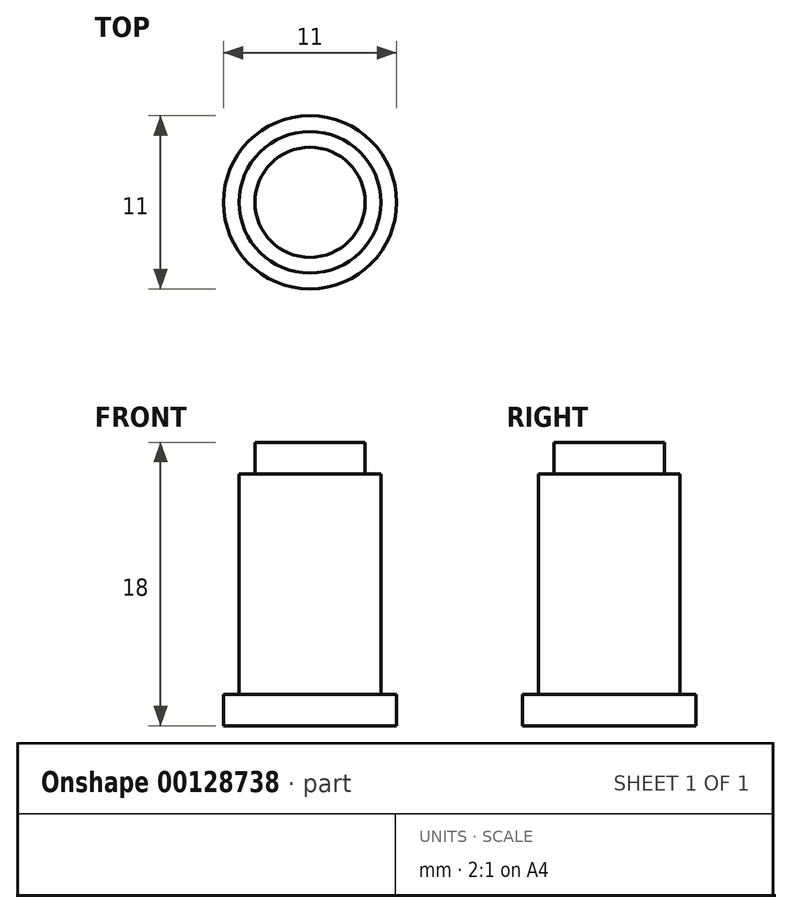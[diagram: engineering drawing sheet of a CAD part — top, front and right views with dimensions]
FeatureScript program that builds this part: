
annotation { "Feature Type Name" : "Feature", "Feature Type Description" : "" }
export const myFeature = defineFeature(function(context is Context, id is Id, definition is map)
    precondition{}
    {
        {
            var Q0;
            Q0=qCreatedBy(makeId("Top.planeOp"),FACE);
            var sketch = newSketch(context, id + "F0", { "sketchPlane" : qUnion([Q0])});
            skCircle(sketch, "E0", {"center": v(0, 0) * mm, "radius": 5.5 * mm});
            skSolve(sketch);
        }
        {
            var Q0;
            Q0=makeQuery(id+"F0.imprint","IMPRINT",FACE,{"disambiguationData":[TD([[makeQuery(id+"F0.imprint","IMPRINT",EDGE,{"derivedFrom":sQuery(id+"F0.wireOp",EDGE,"E0")}),1.0]])]});
            extrude(context, id + "F1", {"entities" : qUnion([Q0]), "depth" : 2 * mm});
        }
        {
            var Q0;
            Q0=makeQuery(id+"F1.opExtrude","CAP_FACE",FACE,{"disambiguationData":[OSD([sQuery(id+"F0.wireOp",EDGE,"E0")])],"isStart":false});
            var sketch = newSketch(context, id + "F2", { "sketchPlane" : qUnion([Q0])});
            skCircle(sketch, "E1", {"center": v(0, 0) * mm, "radius": 4.5 * mm});
            skSolve(sketch);
        }
        {
            var Q0;
            Q0=makeQuery(id+"F2.imprint","IMPRINT",FACE,{"disambiguationData":[TD([[makeQuery(id+"F2.imprint","IMPRINT",EDGE,{"derivedFrom":sQuery(id+"F2.wireOp",EDGE,"E1")}),1.0]])]});
            extrude(context, id + "F3", {"entities" : qUnion([Q0]), "operationType" : NewBodyOperationType.ADD, "depth" : 14 * mm});
        }
        {
            var Q0;
            Q0=makeQuery(id+"F3.opExtrude","CAP_FACE",FACE,{"disambiguationData":[OSD([sQuery(id+"F2.wireOp",EDGE,"E1")])],"isStart":false});
            var sketch = newSketch(context, id + "F4", { "sketchPlane" : qUnion([Q0])});
            skCircle(sketch, "E2", {"center": v(0, 0) * mm, "radius": 3.5 * mm});
            skSolve(sketch);
        }
        {
            var Q0;
            Q0=makeQuery(id+"F4.imprint","IMPRINT",FACE,{"disambiguationData":[TD([[makeQuery(id+"F4.imprint","IMPRINT",EDGE,{"derivedFrom":sQuery(id+"F4.wireOp",EDGE,"E2")}),1.0]])]});
            extrude(context, id + "F5", {"entities" : qUnion([Q0]), "operationType" : NewBodyOperationType.ADD, "depth" : 2 * mm});
        }
    });
